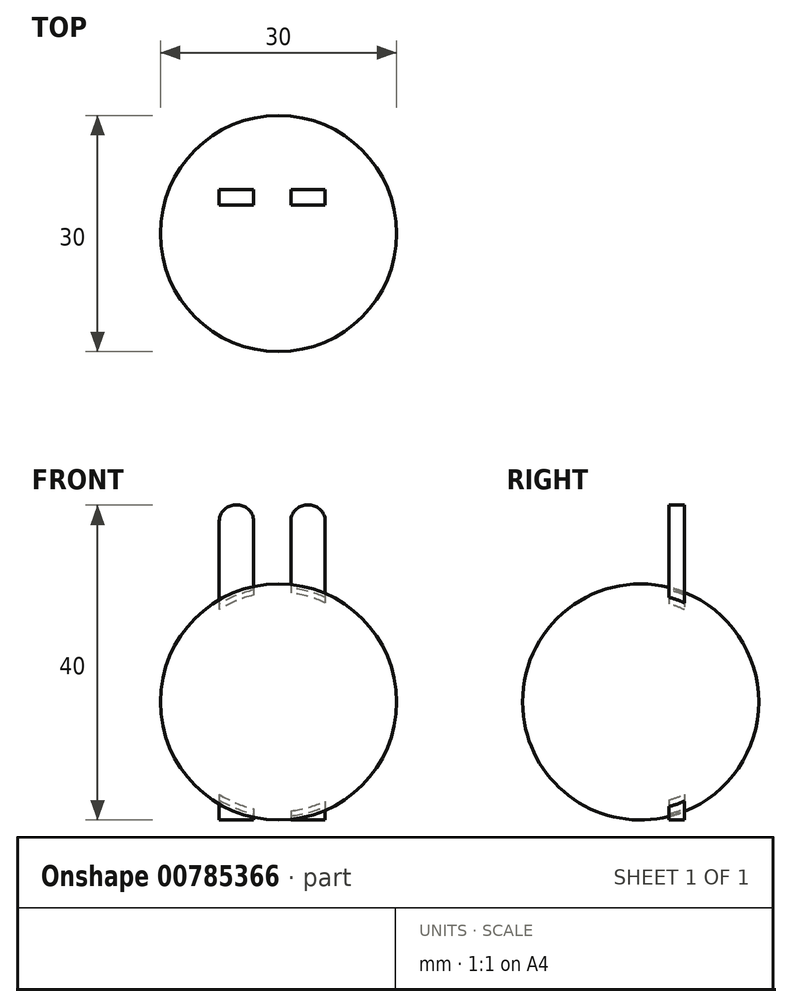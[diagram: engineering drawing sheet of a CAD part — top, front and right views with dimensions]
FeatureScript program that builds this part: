
annotation { "Feature Type Name" : "Feature", "Feature Type Description" : "" }
export const myFeature = defineFeature(function(context is Context, id is Id, definition is map)
    precondition{}
    {
        {
            var Q0;
            Q0=qCreatedBy(makeId("Top.planeOp"),FACE);
            var sketch = newSketch(context, id + "F0", { "sketchPlane" : qUnion([Q0])});
            skLineSegment(sketch, "E0.bottom", {"start": v(15, 15) * mm, "end": v(-15, 15) * mm});
            skLineSegment(sketch, "E0.top", {"start": v(15, -15) * mm, "end": v(-15, -15) * mm});
            skLineSegment(sketch, "E0.left", {"start": v(15, 15) * mm, "end": v(15, -15) * mm});
            skLineSegment(sketch, "E0.right", {"start": v(-15, 15) * mm, "end": v(-15, -15) * mm});
            skPoint(sketch, "E0.middle", {"position": v(0, 0) * mm});
            skSolve(sketch);
        }
        {
            var Q0;
            Q0 = qSketchRegion(id + "F0", true);
            extrude(context, id + "F1", {"entities" : qUnion([Q0]), "depth" : 30 * mm, "offsetDistance" : 25 * mm});
        }
        {
            var Q0;
            Q0=makeQuery(id+"F1.opExtrude","SWEPT_EDGE",EDGE,{"disambiguationData":[OSD([sQuery(id+"F0.wireOp",EDGE,"E0.top"),sQuery(id+"F0.wireOp",EDGE,"E0.right")])]});
            var Q1;
            Q1=makeQuery(id+"F1.opExtrude","CAP_EDGE",EDGE,{"disambiguationData":[OSD([sQuery(id+"F0.wireOp",EDGE,"E0.right")])],"isStart":false});
            var Q2;
            Q2=makeQuery(id+"F1.opExtrude","CAP_EDGE",EDGE,{"disambiguationData":[OSD([sQuery(id+"F0.wireOp",EDGE,"E0.top")])],"isStart":false});
            var Q3;
            Q3=makeQuery(id+"F1.opExtrude","CAP_EDGE",EDGE,{"disambiguationData":[OSD([sQuery(id+"F0.wireOp",EDGE,"E0.bottom")])],"isStart":false});
            var Q4;
            Q4=makeQuery(id+"F1.opExtrude","CAP_EDGE",EDGE,{"disambiguationData":[OSD([sQuery(id+"F0.wireOp",EDGE,"E0.left")])],"isStart":false});
            var Q5;
            Q5=makeQuery(id+"F1.opExtrude","SWEPT_FACE",FACE,{"disambiguationData":[OSD([sQuery(id+"F0.wireOp",EDGE,"E0.bottom")])]});
            var Q6;
            Q6=makeQuery(id+"F1.opExtrude","CAP_EDGE",EDGE,{"disambiguationData":[OSD([sQuery(id+"F0.wireOp",EDGE,"E0.right")])],"isStart":true});
            var Q7;
            Q7=makeQuery(id+"F1.opExtrude","CAP_EDGE",EDGE,{"disambiguationData":[OSD([sQuery(id+"F0.wireOp",EDGE,"E0.top")])],"isStart":true});
            var Q8;
            Q8=makeQuery(id+"F1.opExtrude","CAP_EDGE",EDGE,{"disambiguationData":[OSD([sQuery(id+"F0.wireOp",EDGE,"E0.left")])],"isStart":true});
            var Q9;
            Q9=makeQuery(id+"F1.opExtrude","SWEPT_EDGE",EDGE,{"disambiguationData":[OSD([sQuery(id+"F0.wireOp",EDGE,"E0.top"),sQuery(id+"F0.wireOp",EDGE,"E0.left")])]});
            fillet(context, id + "F2", {"entities" : qUnion([Q0, Q1, Q2, Q3, Q4, Q5, Q6, Q7, Q8, Q9]), "radius" : 15 * mm, "tangentPropagation" : true, "allowEdgeOverflow" : false});
        }
        {
            var Q0;
            Q0=qCreatedBy(makeId("Top.planeOp"),FACE);
            var sketch = newSketch(context, id + "F3", { "sketchPlane" : qUnion([Q0])});
            skLineSegment(sketch, "E1.bottom", {"start": v(5.93, 3.63) * mm, "end": v(1.57, 3.63) * mm});
            skLineSegment(sketch, "E1.top", {"start": v(5.93, 5.56) * mm, "end": v(1.57, 5.56) * mm});
            skLineSegment(sketch, "E1.left", {"start": v(5.93, 3.63) * mm, "end": v(5.93, 5.56) * mm});
            skLineSegment(sketch, "E1.right", {"start": v(1.57, 3.63) * mm, "end": v(1.57, 5.56) * mm});
            skPoint(sketch, "E1.middle", {"position": v(3.75, 4.6) * mm});
            skPoint(sketch, "E2.1.0.0", {"position": v(-5.35, 4.6) * mm});
            skLineSegment(sketch, "E2.1.0.1", {"start": v(-7.53, 3.63) * mm, "end": v(-7.53, 5.56) * mm});
            skLineSegment(sketch, "E2.1.0.2", {"start": v(-3.17, 3.63) * mm, "end": v(-3.17, 5.56) * mm});
            skLineSegment(sketch, "E2.1.0.3", {"start": v(-3.17, 5.56) * mm, "end": v(-7.53, 5.56) * mm});
            skLineSegment(sketch, "E2.1.0.4", {"start": v(-3.17, 3.63) * mm, "end": v(-7.53, 3.63) * mm});
            skPoint(sketch, "E2.2.0.0", {"position": v(-14.45, 4.6) * mm});
            skLineSegment(sketch, "E2.direction1", {"start": v(1.57, 3.63) * mm, "end": v(-7.53, 3.63) * mm, "construction": true});
            skSolve(sketch);
        }
        {
            var Q0;
            Q0 = qSketchRegion(id + "F3", true);
            extrude(context, id + "F4", {"entities" : qUnion([Q0]), "operationType" : NewBodyOperationType.ADD, "depth" : 40 * mm, "offsetDistance" : 25 * mm});
        }
        {
            var Q0;
            Q0=makeQuery(id+"F4.opExtrude","CAP_EDGE",EDGE,{"disambiguationData":[OSD([sQuery(id+"F3.wireOp",EDGE,"E1.left")])],"isStart":false});
            var Q1;
            Q1=makeQuery(id+"F4.opExtrude","CAP_EDGE",EDGE,{"disambiguationData":[OSD([sQuery(id+"F3.wireOp",EDGE,"E2.1.0.2")])],"isStart":false});
            var Q2;
            Q2=makeQuery(id+"F4.opExtrude","CAP_EDGE",EDGE,{"disambiguationData":[OSD([sQuery(id+"F3.wireOp",EDGE,"E1.right")])],"isStart":false});
            var Q3;
            Q3=makeQuery(id+"F4.opExtrude","CAP_EDGE",EDGE,{"disambiguationData":[OSD([sQuery(id+"F3.wireOp",EDGE,"E2.1.0.1")])],"isStart":false});
            fillet(context, id + "F5", {"entities" : qUnion([Q0, Q1, Q2, Q3]), "radius" : 2 * mm, "tangentPropagation" : true, "allowEdgeOverflow" : false});
        }
        {
            var Q0;
            Q0=qCreatedBy(makeId("Front.planeOp"),FACE);
            var sketch = newSketch(context, id + "F6", { "sketchPlane" : qUnion([Q0])});
            skCircle(sketch, "E3", {"center": v(-6.9, 18.87) * mm, "radius": 3.76 * mm});
            skCircle(sketch, "E4.1.0.0", {"center": v(7.2, 18.87) * mm, "radius": 3.76 * mm});
            skLineSegment(sketch, "E4.direction1", {"start": v(-6.9, 18.87) * mm, "end": v(7.2, 18.87) * mm, "construction": true});
            skSolve(sketch);
        }
        {
            var Q0;
            Q0=sQuery(id+"F6.wireOp",EDGE,"E4.1.0.0");
            var Q1;
            Q1=sQuery(id+"F6.wireOp",EDGE,"E3");
            extrude(context, id + "F7", {"bodyType" : ToolBodyType.SURFACE, "surfaceEntities" : qUnion([Q0, Q1]), "depth" : 15.3 * mm, "offsetDistance" : 25 * mm});
        }
    });
